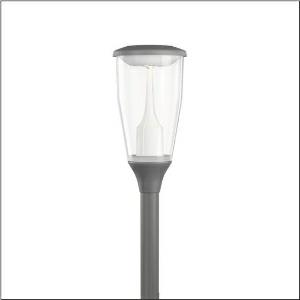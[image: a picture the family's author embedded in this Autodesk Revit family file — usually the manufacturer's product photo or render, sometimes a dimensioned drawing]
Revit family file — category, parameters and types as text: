
# Revit family: dl_11_iq___p1_0a_5xa5575nf14h000022_259a
name_source: partatom
category: Lighting Fixtures
units: mm (PartAtom-declared; Revit-internal decimal feet)

## family parameters
Cut with Voids When Loaded = No
Host = Face
Light Source = No
Part Type = Normal
Room Calculation Point = No
Round Connector Dimension = Use Diameter
Shared = No

## types (1)
- --- (1 x LED, 1530 lm, 11.8 W, 2700K)
    Apparent Load = 12 VA
    CIE Flux Codes = 34 63 91 95 100
    Color Rendering = 70
    Color Temperature = 2700K
    Default Elevation = 1800 mm
    Description = DL 11 iQ, mast luminaire, Module 540 iQ-SR, primary light control with 3 zone facetted reflector, of plastic, silver coated, highly specular, structured, primary optical cover: cover, of PMMA, transparent, light distribution: P1.0a, light emission: direct distribution, primary light characteristic: asymmetric, installation type: post-top, LED, High Power LED, rated luminous flux: 1.560lm, luminous efficacy: 149lm/W, light colour: 727, colour temperature: 2700K, control gear: iQ Street-Remote, control: Street-Remote, Auto-Match, Temp-Guard, Lumen-Switch, Night-Set, Smart-Wire, Light-Fading, Desk-Remote (wireless, voltage-free reading and setting of iQ features in the workshop via application-optimized NFC function/RFID function), optimised constant luminous flux control (CLO 2.0), mains connection: 220..240V, AC, 50/60Hz, connection cable pre-assembled, cable length: 5,5m, wiring characteristics: H07RN-F, 5-core, 1.5mm², start of lifetime: 12W, end of service life: 12W, reduction: 5W, luminaire housing, upper part, of diecast aluminium, coated, SITECO metallic grey (DB 702S), spigot size: 76mm (post-top), mounting height: 3..5m, post-top mast mounting element, of diecast aluminium, coated, SITECO metallic grey (DB 702S), Module 540 iQ-SR, traffic white (RAL 9016), equipment: standard, protection rating (complete): IP66, insulation class (complete): insulation class II (safety insulation), certification: CE, ENEC, ENEC+, VDE, impact resistance: IK07, packaging unit: 1 piece

Light Distribution: P1.0a
    Height = 665 mm
    Lamp = 1 x LED
    Lamp Light Flux = 1530 lm
    Lamp Power = 11.8 W
    Lamp count = 1
    Length = 334 mm
    Luminous efficacy = 130 lm/W
    Manufacturer = Siteco
    ModVariant = No
    Model = 5XA5575NF14H000022
    Number of Poles = 1
    OnlyDefault = Yes
    Power Factor = 1
    Product Name = DL 11 iQ | P1.0a
    Product group = mast luminaire | pylon top
    ProductGroupID = 6100
    Protection Class = Protection class II
    Protection Degree = IP 66
    RLX_Detail_Level = 1
    RLX_Emergency_Light_Flux = 0 lm
    RLX_Emergency_Type = 0
    RLX_Emergency_Type_DB = No
    RlxData = <blob elided: 103605 chars, md5=bc40ded3>
    Socket = socket
    Standby Power = 0 W
    System Light Flux = 1530 lm
    System Power = 12 W
    Type Comments = factory setting: luminous flux: 100 % | dim-lin: 254 | 472 mA
    Type Image = l_1258354.jpg
    URL = http://relux.com
    VarID = @adj_095551
    Voltage = 0 V
    Weight = 0.00 kg
    Width = 0 mm  [stored 0 ft]

note: [stored X ft] marks values corroborated as IEEE doubles in the binary element streams (Revit-internal decimal feet)

## geometry (parser evidence)
native form markers: Blend x4, Sweep x10
no freeform markers — native parametric forms only
